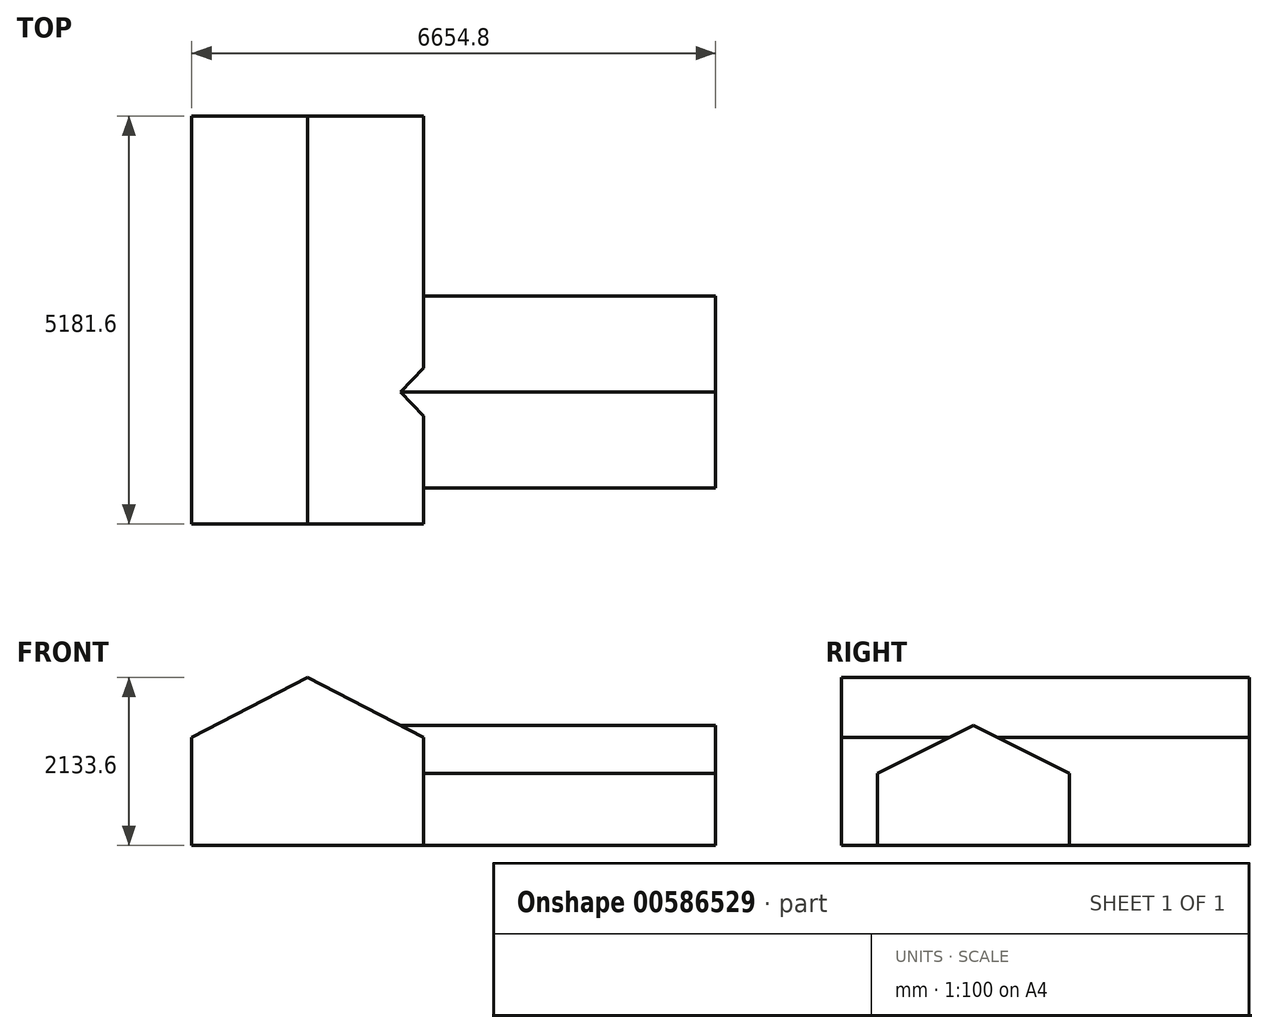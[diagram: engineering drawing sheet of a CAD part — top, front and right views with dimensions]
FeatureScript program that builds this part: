
annotation { "Feature Type Name" : "Feature", "Feature Type Description" : "" }
export const myFeature = defineFeature(function(context is Context, id is Id, definition is map)
    precondition{}
    {
        {
            var Q0;
            Q0=qCreatedBy(makeId("Front.planeOp"),FACE);
            var sketch = newSketch(context, id + "F0", { "sketchPlane" : qUnion([Q0])});
            skLineSegment(sketch, "E0.bottom", {"start": v(-1473.2, 1371.6) * mm, "end": v(1473.2, 1371.6) * mm});
            skLineSegment(sketch, "E0.top", {"start": v(-1473.2, 0) * mm, "end": v(1473.2, 0) * mm});
            skLineSegment(sketch, "E0.left", {"start": v(-1473.2, 1371.6) * mm, "end": v(-1473.2, 0) * mm});
            skLineSegment(sketch, "E0.right", {"start": v(1473.2, 1371.6) * mm, "end": v(1473.2, 0) * mm});
            skPoint(sketch, "E0.middle", {"position": v(0, 0) * mm});
            skLineSegment(sketch, "E1", {"start": v(-1473.2, 1371.6) * mm, "end": v(0, 2133.6) * mm});
            skLineSegment(sketch, "E2", {"start": v(0, 2133.6) * mm, "end": v(1473.2, 1371.6) * mm});
            skSolve(sketch);
        }
        {
            var Q0;
            Q0 = qSketchRegion(id + "F0", true);
            var Q1;
            Q1=sQuery(id+"F0.wireOp",EDGE,"E1");
            var Q2;
            Q2=sQuery(id+"F0.wireOp",EDGE,"E2");
            var Q3;
            Q3=sQuery(id+"F0.wireOp",EDGE,"E0.right");
            var Q4;
            Q4=sQuery(id+"F0.wireOp",EDGE,"E0.top");
            var Q5;
            Q5=sQuery(id+"F0.wireOp",EDGE,"E0.left");
            extrude(context, id + "F1", {"entities" : qUnion([Q0]), "surfaceEntities" : qUnion([Q1, Q2, Q3, Q4, Q5]), "endBound" : BoundingType.SYMMETRIC, "oppositeDirection" : true, "depth" : 5181.6 * mm, "offsetDistance" : 25.4 * mm});
        }
        {
            var Q0;
            Q0=qCreatedBy(makeId("Right.planeOp"),FACE);
            var sketch = newSketch(context, id + "F2", { "sketchPlane" : qUnion([Q0])});
            skLineSegment(sketch, "E3", {"start": v(304.8, 914.4) * mm, "end": v(304.8, 0) * mm});
            skLineSegment(sketch, "E4", {"start": v(-2133.6, 914.4) * mm, "end": v(-2133.6, 0) * mm});
            skLineSegment(sketch, "E5", {"start": v(-2133.6, 914.4) * mm, "end": v(-914.4, 1524) * mm});
            skLineSegment(sketch, "E6", {"start": v(304.8, 914.4) * mm, "end": v(-914.4, 1524) * mm});
            skLineSegment(sketch, "E7", {"start": v(-2133.6, 0) * mm, "end": v(304.8, 0) * mm});
            skSolve(sketch);
        }
        {
            var Q0;
            Q0=makeQuery(id+"F2.imprint","IMPRINT",FACE,{"disambiguationData":[TD([[makeQuery(id+"F2.imprint","IMPRINT",EDGE,{"derivedFrom":sQuery(id+"F2.wireOp",EDGE,"E3")}),-1.0]])]});
            var Q1;
            Q1=sQuery(id+"F2.wireOp",EDGE,"Vyb64SaX-aebg-MSiz-rrQo-TsnZqmhnN6nx");
            var Q2;
            Q2=sQuery(id+"F2.wireOp",EDGE,"1r0y1Nvf-hYmF-WOK0-Uqcs-m05IUppEqU3o");
            var Q3;
            Q3=sQuery(id+"F2.wireOp",EDGE,"cGHoWLQd-Mbvz-fpTa-Ndrb-sNmS6tsoKGWA");
            extrude(context, id + "F3", {"entities" : qUnion([Q0]), "operationType" : NewBodyOperationType.ADD, "surfaceEntities" : qUnion([Q1, Q2, Q3]), "depth" : 5181.6 * mm, "offsetDistance" : 1524 * mm});
        }
    });
